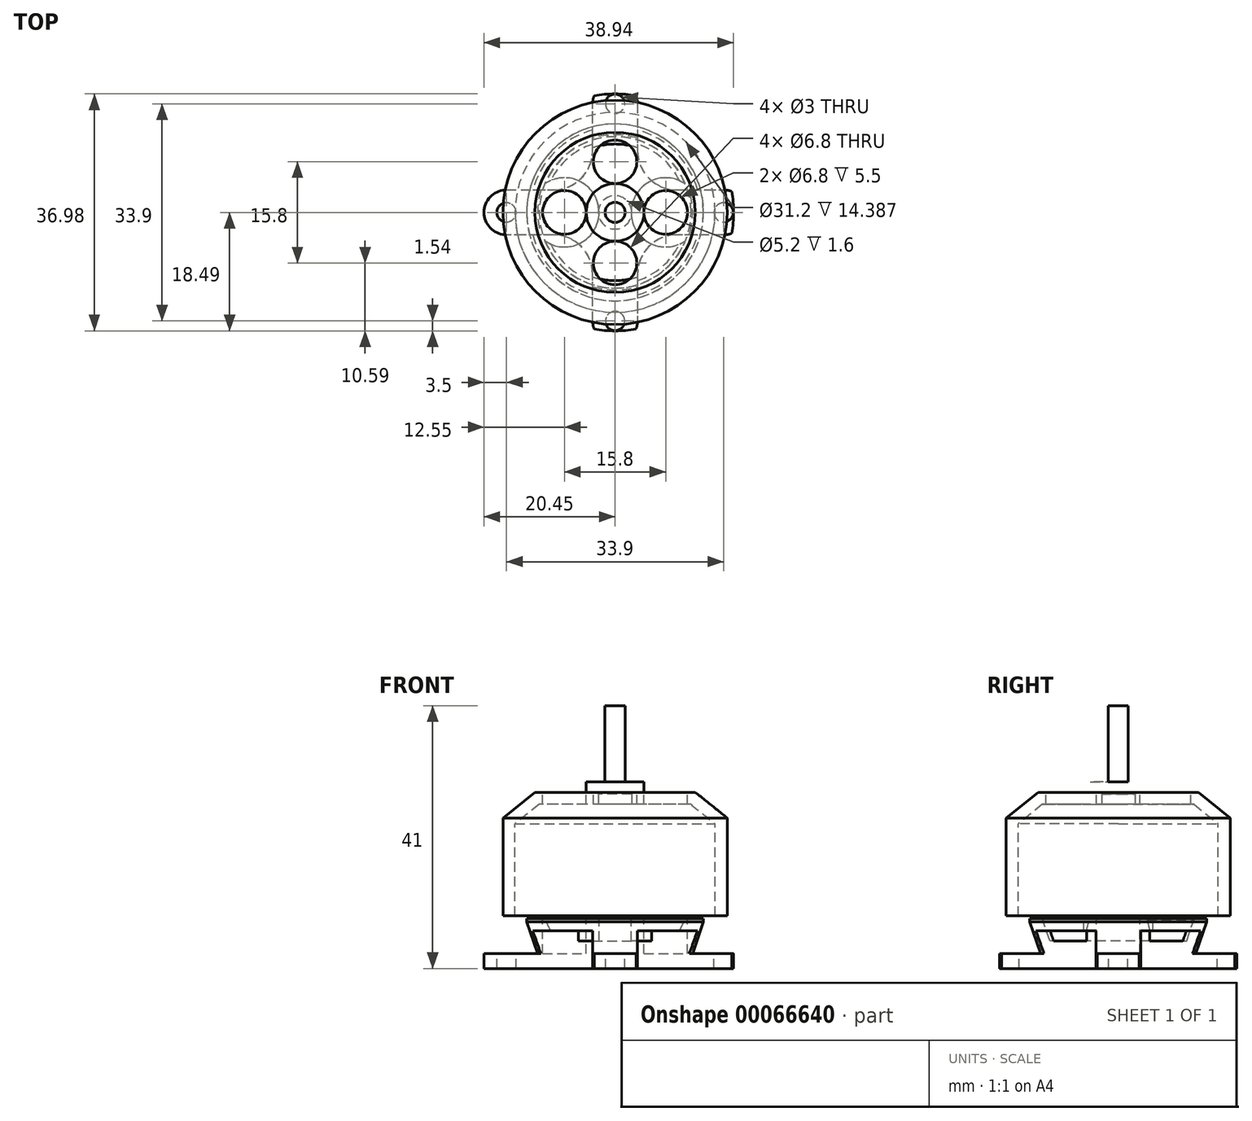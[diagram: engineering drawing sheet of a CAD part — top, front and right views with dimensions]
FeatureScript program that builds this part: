
annotation { "Feature Type Name" : "Feature", "Feature Type Description" : "" }
export const myFeature = defineFeature(function(context is Context, id is Id, definition is map)
    precondition{}
    {
        {
            var Q0;
            Q0=qCreatedBy(makeId("Top.planeOp"),FACE);
            var sketch = newSketch(context, id + "F0", { "sketchPlane" : qUnion([Q0])});
            skCircle(sketch, "E0", {"center": v(0, 0) * mm, "radius": 17.5 * mm});
            skCircle(sketch, "E1", {"center": v(0, 0) * mm, "radius": 1.57 * mm});
            skCircle(sketch, "E2", {"center": v(0, 0) * mm, "radius": 4.5 * mm});
            skCircle(sketch, "E3", {"center": v(0, 0) * mm, "radius": 8.78 * mm});
            skCircle(sketch, "E4", {"center": v(7.9, 0) * mm, "radius": 3.4 * mm});
            skCircle(sketch, "E5.1.0", {"center": v(0, 7.9) * mm, "radius": 3.4 * mm});
            skCircle(sketch, "E5.2.0", {"center": v(-7.9, 0) * mm, "radius": 3.4 * mm});
            skCircle(sketch, "E5.3.0", {"center": v(0, -7.9) * mm, "radius": 3.4 * mm});
            skSolve(sketch);
        }
        {
            var Q0;
            Q0=makeQuery(id+"F0.imprint","IMPRINT",FACE,{"disambiguationData":[TD([[makeQuery(id+"F0.imprint","IMPRINT",EDGE,{"derivedFrom":sQuery(id+"F0.wireOp",EDGE,"E0")}),1.0]])]});
            var Q1;
            {var subQ0=sQuery(id+"F0.wireOp",EDGE,"E5.1.0");var subQ1=sQuery(id+"F0.wireOp",EDGE,"E2");var subQ2=makeQuery(id+"F0.imprint","INTERSECT",VERTEX,{"derivedFrom":[subQ1,subQ0]});Q1=makeQuery(id+"F0.imprint","IMPRINT",FACE,{"disambiguationData":[TD([[makeQuery(id+"F0.imprint","IMPRINT",EDGE,{"disambiguationData":[TD([[subQ2,1.0]])],"derivedFrom":subQ1}),-1.0]])]});}
            var Q2;
            {var subQ0=sQuery(id+"F0.wireOp",EDGE,"E5.1.0");var subQ1=sQuery(id+"F0.wireOp",EDGE,"E2");var subQ2=makeQuery(id+"F0.imprint","INTERSECT",VERTEX,{"derivedFrom":[subQ1,subQ0]});Q2=makeQuery(id+"F0.imprint","IMPRINT",FACE,{"disambiguationData":[TD([[makeQuery(id+"F0.imprint","IMPRINT",EDGE,{"disambiguationData":[TD([[subQ2,-1.0]])],"derivedFrom":subQ1}),-1.0]])]});}
            var Q3;
            Q3=makeQuery(id+"F0.imprint","IMPRINT",FACE,{"disambiguationData":[TD([[makeQuery(id+"F0.imprint","IMPRINT",EDGE,{"derivedFrom":sQuery(id+"F0.wireOp",EDGE,"E1")}),-1.0]])]});
            var Q4;
            {var subQ0=sQuery(id+"F0.wireOp",EDGE,"E4");var subQ1=sQuery(id+"F0.wireOp",EDGE,"E2");var subQ2=makeQuery(id+"F0.imprint","INTERSECT",VERTEX,{"derivedFrom":[subQ1,subQ0]});Q4=makeQuery(id+"F0.imprint","IMPRINT",FACE,{"disambiguationData":[TD([[makeQuery(id+"F0.imprint","IMPRINT",EDGE,{"disambiguationData":[TD([[subQ2,1.0]])],"derivedFrom":subQ1}),-1.0]])]});}
            var Q5;
            {var subQ0=sQuery(id+"F0.wireOp",EDGE,"E5.2.0");var subQ1=sQuery(id+"F0.wireOp",EDGE,"E2");var subQ2=makeQuery(id+"F0.imprint","INTERSECT",VERTEX,{"derivedFrom":[subQ1,subQ0]});Q5=makeQuery(id+"F0.imprint","IMPRINT",FACE,{"disambiguationData":[TD([[makeQuery(id+"F0.imprint","IMPRINT",EDGE,{"disambiguationData":[TD([[subQ2,-1.0]])],"derivedFrom":subQ1}),-1.0]])]});}
            var Q6;
            Q6=makeQuery(id+"F0.imprint","IMPRINT",FACE,{"disambiguationData":[TD([[makeQuery(id+"F0.imprint","IMPRINT",EDGE,{"derivedFrom":sQuery(id+"F0.wireOp",EDGE,"E1")}),1.0]])]});
            var Q7;
            {var subQ0=sQuery(id+"F0.wireOp",EDGE,"E5.2.0");var subQ1=sQuery(id+"F0.wireOp",EDGE,"E3");var subQ2=makeQuery(id+"F0.imprint","INTERSECT",VERTEX,{"disambiguationData":[OD(0.0)],"derivedFrom":[subQ1,subQ0]});Q7=makeQuery(id+"F0.imprint","IMPRINT",FACE,{"disambiguationData":[TD([[makeQuery(id+"F0.imprint","IMPRINT",EDGE,{"disambiguationData":[TD([[subQ2,-1.0]])],"derivedFrom":subQ1}),-1.0]])]});}
            var Q8;
            {var subQ0=sQuery(id+"F0.wireOp",EDGE,"E5.2.0");var subQ1=sQuery(id+"F0.wireOp",EDGE,"E3");var subQ2=makeQuery(id+"F0.imprint","INTERSECT",VERTEX,{"disambiguationData":[OD(0.0)],"derivedFrom":[subQ1,subQ0]});Q8=makeQuery(id+"F0.imprint","IMPRINT",FACE,{"disambiguationData":[TD([[makeQuery(id+"F0.imprint","IMPRINT",EDGE,{"disambiguationData":[TD([[subQ2,-1.0]])],"derivedFrom":subQ1}),1.0]])]});}
            var Q9;
            {var subQ0=sQuery(id+"F0.wireOp",EDGE,"E5.1.0");var subQ1=sQuery(id+"F0.wireOp",EDGE,"E3");var subQ2=makeQuery(id+"F0.imprint","INTERSECT",VERTEX,{"disambiguationData":[OD(0.0)],"derivedFrom":[subQ1,subQ0]});Q9=makeQuery(id+"F0.imprint","IMPRINT",FACE,{"disambiguationData":[TD([[makeQuery(id+"F0.imprint","IMPRINT",EDGE,{"disambiguationData":[TD([[subQ2,-1.0]])],"derivedFrom":subQ1}),1.0]])]});}
            var Q10;
            {var subQ0=sQuery(id+"F0.wireOp",EDGE,"E4");var subQ1=sQuery(id+"F0.wireOp",EDGE,"E3");var subQ2=makeQuery(id+"F0.imprint","INTERSECT",VERTEX,{"disambiguationData":[OD(0.0)],"derivedFrom":[subQ1,subQ0]});Q10=makeQuery(id+"F0.imprint","IMPRINT",FACE,{"disambiguationData":[TD([[makeQuery(id+"F0.imprint","IMPRINT",EDGE,{"disambiguationData":[TD([[subQ2,1.0]])],"derivedFrom":subQ1}),1.0]])]});}
            var Q11;
            {var subQ0=sQuery(id+"F0.wireOp",EDGE,"E4");var subQ1=sQuery(id+"F0.wireOp",EDGE,"E3");var subQ2=makeQuery(id+"F0.imprint","INTERSECT",VERTEX,{"disambiguationData":[OD(0.0)],"derivedFrom":[subQ1,subQ0]});Q11=makeQuery(id+"F0.imprint","IMPRINT",FACE,{"disambiguationData":[TD([[makeQuery(id+"F0.imprint","IMPRINT",EDGE,{"disambiguationData":[TD([[subQ2,1.0]])],"derivedFrom":subQ1}),-1.0]])]});}
            var Q12;
            {var subQ0=sQuery(id+"F0.wireOp",EDGE,"E5.3.0");var subQ1=sQuery(id+"F0.wireOp",EDGE,"E3");var subQ2=makeQuery(id+"F0.imprint","INTERSECT",VERTEX,{"disambiguationData":[OD(0.0)],"derivedFrom":[subQ1,subQ0]});Q12=makeQuery(id+"F0.imprint","IMPRINT",FACE,{"disambiguationData":[TD([[makeQuery(id+"F0.imprint","IMPRINT",EDGE,{"disambiguationData":[TD([[subQ2,-1.0]])],"derivedFrom":subQ1}),1.0]])]});}
            var Q13;
            {var subQ0=sQuery(id+"F0.wireOp",EDGE,"E5.1.0");var subQ1=sQuery(id+"F0.wireOp",EDGE,"E3");var subQ2=makeQuery(id+"F0.imprint","INTERSECT",VERTEX,{"disambiguationData":[OD(0.0)],"derivedFrom":[subQ1,subQ0]});Q13=makeQuery(id+"F0.imprint","IMPRINT",FACE,{"disambiguationData":[TD([[makeQuery(id+"F0.imprint","IMPRINT",EDGE,{"disambiguationData":[TD([[subQ2,-1.0]])],"derivedFrom":subQ1}),-1.0]])]});}
            var Q14;
            {var subQ0=sQuery(id+"F0.wireOp",EDGE,"E5.3.0");var subQ1=sQuery(id+"F0.wireOp",EDGE,"E3");var subQ2=makeQuery(id+"F0.imprint","INTERSECT",VERTEX,{"disambiguationData":[OD(0.0)],"derivedFrom":[subQ1,subQ0]});Q14=makeQuery(id+"F0.imprint","IMPRINT",FACE,{"disambiguationData":[TD([[makeQuery(id+"F0.imprint","IMPRINT",EDGE,{"disambiguationData":[TD([[subQ2,-1.0]])],"derivedFrom":subQ1}),-1.0]])]});}
            extrude(context, id + "F1", {"entities" : qUnion([Q0, Q1, Q2, Q3, Q4, Q5, Q6, Q7, Q8, Q9, Q10, Q11, Q12, Q13, Q14]), "oppositeDirection" : true, "depth" : 19.3 * mm});
        }
        {
            var Q0;
            Q0=makeQuery(id+"F1.opExtrude","CAP_EDGE",EDGE,{"disambiguationData":[OSD([sQuery(id+"F0.wireOp",EDGE,"E0")])],"isStart":true});
            chamfer(context, id + "F2", {"entities" : qUnion([Q0]), "chamferType" : ChamferType.TWO_OFFSETS, "width1" : 5 * mm, "oppositeDirection" : false, "width2" : 4 * mm, "tangentPropagation" : true});
        }
        {
            var Q0;
            Q0=makeQuery(id+"F0.imprint","IMPRINT",FACE,{"disambiguationData":[TD([[makeQuery(id+"F0.imprint","IMPRINT",EDGE,{"derivedFrom":sQuery(id+"F0.wireOp",EDGE,"E1")}),-1.0]])]});
            extrude(context, id + "F3", {"entities" : qUnion([Q0]), "operationType" : NewBodyOperationType.ADD, "depth" : 1.6 * mm});
        }
        {
            var Q0;
            Q0=makeQuery(id+"F0.imprint","IMPRINT",FACE,{"disambiguationData":[TD([[makeQuery(id+"F0.imprint","IMPRINT",EDGE,{"derivedFrom":sQuery(id+"F0.wireOp",EDGE,"E1")}),1.0]])]});
            var Q1;
            Q1=sQuery(id+"F0.wireOp",EDGE,"E1");
            extrude(context, id + "F4", {"entities" : qUnion([Q0]), "operationType" : NewBodyOperationType.ADD, "surfaceEntities" : qUnion([Q1]), "depth" : 13.5 * mm});
        }
        {
            var Q0;
            Q0=makeQuery(id+"F1.opExtrude","CAP_FACE",FACE,{"disambiguationData":[OSD([sQuery(id+"F0.wireOp",EDGE,"E0")])],"isStart":false});
            shell(context, id + "F5", {"entities" : qUnion([Q0]), "thickness" : 1.9 * mm});
        }
        {
            var Q0;
            {var subQ0=sQuery(id+"F0.wireOp",EDGE,"E5.3.0");var subQ1=sQuery(id+"F0.wireOp",EDGE,"E3");var subQ2=makeQuery(id+"F0.imprint","INTERSECT",VERTEX,{"disambiguationData":[OD(0.0)],"derivedFrom":[subQ1,subQ0]});Q0=makeQuery(id+"F0.imprint","IMPRINT",FACE,{"disambiguationData":[TD([[makeQuery(id+"F0.imprint","IMPRINT",EDGE,{"disambiguationData":[TD([[subQ2,-1.0]])],"derivedFrom":subQ1}),-1.0]])]});}
            var Q1;
            {var subQ0=sQuery(id+"F0.wireOp",EDGE,"E5.3.0");var subQ1=sQuery(id+"F0.wireOp",EDGE,"E3");var subQ2=makeQuery(id+"F0.imprint","INTERSECT",VERTEX,{"disambiguationData":[OD(0.0)],"derivedFrom":[subQ1,subQ0]});Q1=makeQuery(id+"F0.imprint","IMPRINT",FACE,{"disambiguationData":[TD([[makeQuery(id+"F0.imprint","IMPRINT",EDGE,{"disambiguationData":[TD([[subQ2,-1.0]])],"derivedFrom":subQ1}),1.0]])]});}
            var Q2;
            {var subQ0=sQuery(id+"F0.wireOp",EDGE,"E4");var subQ1=sQuery(id+"F0.wireOp",EDGE,"E3");var subQ2=makeQuery(id+"F0.imprint","INTERSECT",VERTEX,{"disambiguationData":[OD(0.0)],"derivedFrom":[subQ1,subQ0]});Q2=makeQuery(id+"F0.imprint","IMPRINT",FACE,{"disambiguationData":[TD([[makeQuery(id+"F0.imprint","IMPRINT",EDGE,{"disambiguationData":[TD([[subQ2,1.0]])],"derivedFrom":subQ1}),-1.0]])]});}
            var Q3;
            {var subQ0=sQuery(id+"F0.wireOp",EDGE,"E4");var subQ1=sQuery(id+"F0.wireOp",EDGE,"E3");var subQ2=makeQuery(id+"F0.imprint","INTERSECT",VERTEX,{"disambiguationData":[OD(0.0)],"derivedFrom":[subQ1,subQ0]});Q3=makeQuery(id+"F0.imprint","IMPRINT",FACE,{"disambiguationData":[TD([[makeQuery(id+"F0.imprint","IMPRINT",EDGE,{"disambiguationData":[TD([[subQ2,1.0]])],"derivedFrom":subQ1}),1.0]])]});}
            var Q4;
            {var subQ0=sQuery(id+"F0.wireOp",EDGE,"E5.1.0");var subQ1=sQuery(id+"F0.wireOp",EDGE,"E3");var subQ2=makeQuery(id+"F0.imprint","INTERSECT",VERTEX,{"disambiguationData":[OD(0.0)],"derivedFrom":[subQ1,subQ0]});Q4=makeQuery(id+"F0.imprint","IMPRINT",FACE,{"disambiguationData":[TD([[makeQuery(id+"F0.imprint","IMPRINT",EDGE,{"disambiguationData":[TD([[subQ2,-1.0]])],"derivedFrom":subQ1}),1.0]])]});}
            var Q5;
            {var subQ0=sQuery(id+"F0.wireOp",EDGE,"E5.1.0");var subQ1=sQuery(id+"F0.wireOp",EDGE,"E3");var subQ2=makeQuery(id+"F0.imprint","INTERSECT",VERTEX,{"disambiguationData":[OD(0.0)],"derivedFrom":[subQ1,subQ0]});Q5=makeQuery(id+"F0.imprint","IMPRINT",FACE,{"disambiguationData":[TD([[makeQuery(id+"F0.imprint","IMPRINT",EDGE,{"disambiguationData":[TD([[subQ2,-1.0]])],"derivedFrom":subQ1}),-1.0]])]});}
            var Q6;
            {var subQ0=sQuery(id+"F0.wireOp",EDGE,"E5.2.0");var subQ1=sQuery(id+"F0.wireOp",EDGE,"E3");var subQ2=makeQuery(id+"F0.imprint","INTERSECT",VERTEX,{"disambiguationData":[OD(0.0)],"derivedFrom":[subQ1,subQ0]});Q6=makeQuery(id+"F0.imprint","IMPRINT",FACE,{"disambiguationData":[TD([[makeQuery(id+"F0.imprint","IMPRINT",EDGE,{"disambiguationData":[TD([[subQ2,-1.0]])],"derivedFrom":subQ1}),1.0]])]});}
            var Q7;
            {var subQ0=sQuery(id+"F0.wireOp",EDGE,"E5.2.0");var subQ1=sQuery(id+"F0.wireOp",EDGE,"E3");var subQ2=makeQuery(id+"F0.imprint","INTERSECT",VERTEX,{"disambiguationData":[OD(0.0)],"derivedFrom":[subQ1,subQ0]});Q7=makeQuery(id+"F0.imprint","IMPRINT",FACE,{"disambiguationData":[TD([[makeQuery(id+"F0.imprint","IMPRINT",EDGE,{"disambiguationData":[TD([[subQ2,-1.0]])],"derivedFrom":subQ1}),-1.0]])]});}
            var Q8;
            Q8=sQuery(id+"F0.wireOp",EDGE,"E5.3.0");
            extrude(context, id + "F6", {"entities" : qUnion([Q0, Q1, Q2, Q3, Q4, Q5, Q6, Q7]), "operationType" : NewBodyOperationType.REMOVE, "surfaceEntities" : qUnion([Q8]), "endBound" : BoundingType.THROUGH_ALL, "oppositeDirection" : true, "depth" : 25 * mm});
        }
        {
            var Q0;
            Q0=qCreatedBy(makeId("Top.planeOp"),FACE);
            var sketch = newSketch(context, id + "F7", { "sketchPlane" : qUnion([Q0])});
            skCircle(sketch, "E6", {"center": v(16.95, 0) * mm, "radius": 3.5 * mm});
            skCircle(sketch, "E7.1.0", {"center": v(0, 16.95) * mm, "radius": 3.5 * mm});
            skCircle(sketch, "E7.2.0", {"center": v(-16.95, 0) * mm, "radius": 3.5 * mm});
            skCircle(sketch, "E7.3.0", {"center": v(0, -16.95) * mm, "radius": 3.5 * mm});
            skPoint(sketch, "E7.center", {"position": v(0, 0) * mm});
            skLineSegment(sketch, "E8", {"start": v(16.95, 3.5) * mm, "end": v(9.66, 3.5) * mm});
            skLineSegment(sketch, "E9", {"start": v(3.5, 9.66) * mm, "end": v(3.5, 16.95) * mm});
            skPoint(sketch, "E10.visualSharp", {"position": v(3.5, 3.5) * mm});
            skArc(sketch, "E10.filletArc", {"start": v(3.5, 9.66) * mm, "mid": v(5.3, 5.3) * mm, "end": v(9.66, 3.5) * mm});
            skLineSegment(sketch, "E11.1.0", {"start": v(-3.5, 16.95) * mm, "end": v(-3.5, 9.66) * mm});
            skArc(sketch, "E11.1.1", {"start": v(-9.66, 3.5) * mm, "mid": v(-5.3, 5.3) * mm, "end": v(-3.5, 9.66) * mm});
            skLineSegment(sketch, "E11.1.2", {"start": v(-9.66, 3.5) * mm, "end": v(-16.95, 3.5) * mm});
            skLineSegment(sketch, "E11.2.0", {"start": v(-16.95, -3.5) * mm, "end": v(-9.66, -3.5) * mm});
            skArc(sketch, "E11.2.1", {"start": v(-3.5, -9.66) * mm, "mid": v(-5.3, -5.3) * mm, "end": v(-9.66, -3.5) * mm});
            skLineSegment(sketch, "E11.2.2", {"start": v(-3.5, -9.66) * mm, "end": v(-3.5, -16.95) * mm});
            skLineSegment(sketch, "E11.3.0", {"start": v(3.5, -16.95) * mm, "end": v(3.5, -9.66) * mm});
            skArc(sketch, "E11.3.1", {"start": v(9.66, -3.5) * mm, "mid": v(5.3, -5.3) * mm, "end": v(3.5, -9.66) * mm});
            skLineSegment(sketch, "E11.3.2", {"start": v(9.66, -3.5) * mm, "end": v(16.95, -3.5) * mm});
            skSolve(sketch);
        }
        {
            var Q0;
            Q0=makeQuery(id+"F1.opExtrude","CAP_FACE",FACE,{"disambiguationData":[OSD([sQuery(id+"F0.wireOp",EDGE,"E0")])],"isStart":false});
            cPlane(context, id + "F8", {"entities" : qUnion([Q0]), "cplaneType" : CPlaneType.OFFSET, "offset" : .4 * mm, "width" : 150 * mm, "height" : 150 * mm});
        }
        {
            var Q0;
            Q0=qCreatedBy(id+"F8.planeOp",FACE);
            var sketch = newSketch(context, id + "F9", { "sketchPlane" : qUnion([Q0])});
            skCircle(sketch, "E12", {"center": v(0, 0) * mm, "radius": 13.8 * mm});
            skCircle(sketch, "E13", {"center": v(0, 0) * mm, "radius": 1.57 * mm});
            skCircle(sketch, "E14", {"center": v(0, 0) * mm, "radius": 4.5 * mm});
            skCircle(sketch, "E15", {"center": v(0, 0) * mm, "radius": 8.78 * mm});
            skCircle(sketch, "E16", {"center": v(7.9, 0) * mm, "radius": 3.4 * mm});
            skCircle(sketch, "E17.1.0", {"center": v(0, 7.9) * mm, "radius": 3.4 * mm});
            skCircle(sketch, "E17.2.0", {"center": v(-7.9, 0) * mm, "radius": 3.4 * mm});
            skCircle(sketch, "E17.3.0", {"center": v(0, -7.9) * mm, "radius": 3.4 * mm});
            skSolve(sketch);
        }
        {
            var Q0;
            Q0=makeQuery(id+"F9.imprint","IMPRINT",FACE,{"disambiguationData":[TD([[makeQuery(id+"F9.imprint","IMPRINT",EDGE,{"derivedFrom":sQuery(id+"F9.wireOp",EDGE,"E12")}),1.0]])]});
            var Q1;
            {var subQ0=sQuery(id+"F9.wireOp",EDGE,"E17.3.0");var subQ1=sQuery(id+"F9.wireOp",EDGE,"E15");var subQ2=makeQuery(id+"F9.imprint","INTERSECT",VERTEX,{"disambiguationData":[OD(0.0)],"derivedFrom":[subQ1,subQ0]});Q1=makeQuery(id+"F9.imprint","IMPRINT",FACE,{"disambiguationData":[TD([[makeQuery(id+"F9.imprint","IMPRINT",EDGE,{"disambiguationData":[TD([[subQ2,-1.0]])],"derivedFrom":subQ1}),-1.0]])]});}
            var Q2;
            {var subQ0=sQuery(id+"F9.wireOp",EDGE,"E17.3.0");var subQ1=sQuery(id+"F9.wireOp",EDGE,"E15");var subQ2=makeQuery(id+"F9.imprint","INTERSECT",VERTEX,{"disambiguationData":[OD(0.0)],"derivedFrom":[subQ1,subQ0]});Q2=makeQuery(id+"F9.imprint","IMPRINT",FACE,{"disambiguationData":[TD([[makeQuery(id+"F9.imprint","IMPRINT",EDGE,{"disambiguationData":[TD([[subQ2,-1.0]])],"derivedFrom":subQ1}),1.0]])]});}
            var Q3;
            {var subQ0=sQuery(id+"F9.wireOp",EDGE,"E17.2.0");var subQ1=sQuery(id+"F9.wireOp",EDGE,"E15");var subQ2=makeQuery(id+"F9.imprint","INTERSECT",VERTEX,{"disambiguationData":[OD(0.0)],"derivedFrom":[subQ1,subQ0]});Q3=makeQuery(id+"F9.imprint","IMPRINT",FACE,{"disambiguationData":[TD([[makeQuery(id+"F9.imprint","IMPRINT",EDGE,{"disambiguationData":[TD([[subQ2,-1.0]])],"derivedFrom":subQ1}),-1.0]])]});}
            var Q4;
            {var subQ0=sQuery(id+"F9.wireOp",EDGE,"E17.2.0");var subQ1=sQuery(id+"F9.wireOp",EDGE,"E15");var subQ2=makeQuery(id+"F9.imprint","INTERSECT",VERTEX,{"disambiguationData":[OD(0.0)],"derivedFrom":[subQ1,subQ0]});Q4=makeQuery(id+"F9.imprint","IMPRINT",FACE,{"disambiguationData":[TD([[makeQuery(id+"F9.imprint","IMPRINT",EDGE,{"disambiguationData":[TD([[subQ2,-1.0]])],"derivedFrom":subQ1}),1.0]])]});}
            var Q5;
            {var subQ0=sQuery(id+"F9.wireOp",EDGE,"E17.1.0");var subQ1=sQuery(id+"F9.wireOp",EDGE,"E14");var subQ2=makeQuery(id+"F9.imprint","INTERSECT",VERTEX,{"derivedFrom":[subQ1,subQ0]});Q5=makeQuery(id+"F9.imprint","IMPRINT",FACE,{"disambiguationData":[TD([[makeQuery(id+"F9.imprint","IMPRINT",EDGE,{"disambiguationData":[TD([[subQ2,-1.0]])],"derivedFrom":subQ1}),-1.0]])]});}
            var Q6;
            {var subQ0=sQuery(id+"F9.wireOp",EDGE,"E17.2.0");var subQ1=sQuery(id+"F9.wireOp",EDGE,"E14");var subQ2=makeQuery(id+"F9.imprint","INTERSECT",VERTEX,{"derivedFrom":[subQ1,subQ0]});Q6=makeQuery(id+"F9.imprint","IMPRINT",FACE,{"disambiguationData":[TD([[makeQuery(id+"F9.imprint","IMPRINT",EDGE,{"disambiguationData":[TD([[subQ2,-1.0]])],"derivedFrom":subQ1}),-1.0]])]});}
            var Q7;
            Q7=makeQuery(id+"F9.imprint","IMPRINT",FACE,{"disambiguationData":[TD([[makeQuery(id+"F9.imprint","IMPRINT",EDGE,{"derivedFrom":sQuery(id+"F9.wireOp",EDGE,"E13")}),-1.0]])]});
            var Q8;
            Q8=makeQuery(id+"F9.imprint","IMPRINT",FACE,{"disambiguationData":[TD([[makeQuery(id+"F9.imprint","IMPRINT",EDGE,{"derivedFrom":sQuery(id+"F9.wireOp",EDGE,"E13")}),1.0]])]});
            var Q9;
            {var subQ0=sQuery(id+"F9.wireOp",EDGE,"E16");var subQ1=sQuery(id+"F9.wireOp",EDGE,"E14");var subQ2=makeQuery(id+"F9.imprint","INTERSECT",VERTEX,{"derivedFrom":[subQ1,subQ0]});Q9=makeQuery(id+"F9.imprint","IMPRINT",FACE,{"disambiguationData":[TD([[makeQuery(id+"F9.imprint","IMPRINT",EDGE,{"disambiguationData":[TD([[subQ2,1.0]])],"derivedFrom":subQ1}),-1.0]])]});}
            var Q10;
            {var subQ0=sQuery(id+"F9.wireOp",EDGE,"E16");var subQ1=sQuery(id+"F9.wireOp",EDGE,"E15");var subQ2=makeQuery(id+"F9.imprint","INTERSECT",VERTEX,{"disambiguationData":[OD(0.0)],"derivedFrom":[subQ1,subQ0]});Q10=makeQuery(id+"F9.imprint","IMPRINT",FACE,{"disambiguationData":[TD([[makeQuery(id+"F9.imprint","IMPRINT",EDGE,{"disambiguationData":[TD([[subQ2,1.0]])],"derivedFrom":subQ1}),1.0]])]});}
            var Q11;
            {var subQ0=sQuery(id+"F9.wireOp",EDGE,"E16");var subQ1=sQuery(id+"F9.wireOp",EDGE,"E15");var subQ2=makeQuery(id+"F9.imprint","INTERSECT",VERTEX,{"disambiguationData":[OD(0.0)],"derivedFrom":[subQ1,subQ0]});Q11=makeQuery(id+"F9.imprint","IMPRINT",FACE,{"disambiguationData":[TD([[makeQuery(id+"F9.imprint","IMPRINT",EDGE,{"disambiguationData":[TD([[subQ2,1.0]])],"derivedFrom":subQ1}),-1.0]])]});}
            var Q12;
            {var subQ0=sQuery(id+"F9.wireOp",EDGE,"E17.1.0");var subQ1=sQuery(id+"F9.wireOp",EDGE,"E14");var subQ2=makeQuery(id+"F9.imprint","INTERSECT",VERTEX,{"derivedFrom":[subQ1,subQ0]});Q12=makeQuery(id+"F9.imprint","IMPRINT",FACE,{"disambiguationData":[TD([[makeQuery(id+"F9.imprint","IMPRINT",EDGE,{"disambiguationData":[TD([[subQ2,1.0]])],"derivedFrom":subQ1}),-1.0]])]});}
            var Q13;
            {var subQ0=sQuery(id+"F9.wireOp",EDGE,"E17.1.0");var subQ1=sQuery(id+"F9.wireOp",EDGE,"E15");var subQ2=makeQuery(id+"F9.imprint","INTERSECT",VERTEX,{"disambiguationData":[OD(0.0)],"derivedFrom":[subQ1,subQ0]});Q13=makeQuery(id+"F9.imprint","IMPRINT",FACE,{"disambiguationData":[TD([[makeQuery(id+"F9.imprint","IMPRINT",EDGE,{"disambiguationData":[TD([[subQ2,-1.0]])],"derivedFrom":subQ1}),1.0]])]});}
            var Q14;
            {var subQ0=sQuery(id+"F9.wireOp",EDGE,"E17.1.0");var subQ1=sQuery(id+"F9.wireOp",EDGE,"E15");var subQ2=makeQuery(id+"F9.imprint","INTERSECT",VERTEX,{"disambiguationData":[OD(0.0)],"derivedFrom":[subQ1,subQ0]});Q14=makeQuery(id+"F9.imprint","IMPRINT",FACE,{"disambiguationData":[TD([[makeQuery(id+"F9.imprint","IMPRINT",EDGE,{"disambiguationData":[TD([[subQ2,-1.0]])],"derivedFrom":subQ1}),-1.0]])]});}
            extrude(context, id + "F10", {"entities" : qUnion([Q0, Q1, Q2, Q3, Q4, Q5, Q6, Q7, Q8, Q9, Q10, Q11, Q12, Q13, Q14]), "operationType" : NewBodyOperationType.ADD, "depth" : 5.5 * mm});
        }
        {
            var Q0;
            Q0=makeQuery(id+"F10.opExtrude","CAP_EDGE",EDGE,{"disambiguationData":[OSD([sQuery(id+"F9.wireOp",EDGE,"E12")])],"isStart":false});
            chamfer(context, id + "F11", {"entities" : qUnion([Q0]), "chamferType" : ChamferType.TWO_OFFSETS, "width1" : 5 * mm, "oppositeDirection" : true, "width2" : 1.7 * mm, "tangentPropagation" : true});
        }
        {
            var Q0;
            Q0=makeQuery(id+"F10.opExtrude","CAP_FACE",FACE,{"disambiguationData":[OSD([sQuery(id+"F9.wireOp",EDGE,"E12")])],"isStart":true});
            shell(context, id + "F12", {"entities" : qUnion([Q0]), "thickness" : 2 * mm});
        }
        {
            var Q0;
            Q0=makeQuery(id+"F10.opExtrude","CAP_FACE",FACE,{"disambiguationData":[OSD([sQuery(id+"F9.wireOp",EDGE,"E12")])],"isStart":false});
            cPlane(context, id + "F13", {"entities" : qUnion([Q0]), "cplaneType" : CPlaneType.OFFSET, "offset" : 0 * mm, "width" : 150 * mm, "height" : 150 * mm});
        }
        {
            var Q0;
            Q0=qCreatedBy(id+"F13.planeOp",FACE);
            var sketch = newSketch(context, id + "F14", { "sketchPlane" : qUnion([Q0])});
            skCircle(sketch, "E18", {"center": v(16.95, 0) * mm, "radius": 3.5 * mm});
            skCircle(sketch, "E19.1.0", {"center": v(0, 16.95) * mm, "radius": 3.5 * mm});
            skCircle(sketch, "E19.2.0", {"center": v(-16.95, 0) * mm, "radius": 3.5 * mm});
            skCircle(sketch, "E19.3.0", {"center": v(0, -16.95) * mm, "radius": 3.5 * mm});
            skPoint(sketch, "E19.center", {"position": v(0, 0) * mm});
            skLineSegment(sketch, "E20", {"start": v(16.95, 3.5) * mm, "end": v(9.66, 3.5) * mm});
            skLineSegment(sketch, "E21", {"start": v(3.5, 9.66) * mm, "end": v(3.5, 16.95) * mm});
            skPoint(sketch, "E22.visualSharp", {"position": v(3.5, 3.5) * mm});
            skArc(sketch, "E22.filletArc", {"start": v(3.5, 9.66) * mm, "mid": v(5.3, 5.3) * mm, "end": v(9.66, 3.5) * mm});
            skLineSegment(sketch, "E23.1.0", {"start": v(-3.5, 16.95) * mm, "end": v(-3.5, 9.66) * mm});
            skArc(sketch, "E23.1.1", {"start": v(-9.66, 3.5) * mm, "mid": v(-5.3, 5.3) * mm, "end": v(-3.5, 9.66) * mm});
            skLineSegment(sketch, "E23.1.2", {"start": v(-9.66, 3.5) * mm, "end": v(-16.95, 3.5) * mm});
            skLineSegment(sketch, "E23.2.0", {"start": v(-16.95, -3.5) * mm, "end": v(-9.66, -3.5) * mm});
            skArc(sketch, "E23.2.1", {"start": v(-3.5, -9.66) * mm, "mid": v(-5.3, -5.3) * mm, "end": v(-9.66, -3.5) * mm});
            skLineSegment(sketch, "E23.2.2", {"start": v(-3.5, -9.66) * mm, "end": v(-3.5, -16.95) * mm});
            skLineSegment(sketch, "E23.3.0", {"start": v(3.5, -16.95) * mm, "end": v(3.5, -9.66) * mm});
            skArc(sketch, "E23.3.1", {"start": v(9.66, -3.5) * mm, "mid": v(5.3, -5.3) * mm, "end": v(3.5, -9.66) * mm});
            skLineSegment(sketch, "E23.3.2", {"start": v(9.66, -3.5) * mm, "end": v(16.95, -3.5) * mm});
            skCircle(sketch, "E24", {"center": v(0, 0) * mm, "radius": 18.5 * mm});
            skCircle(sketch, "E25", {"center": v(16.95, 0) * mm, "radius": 1.5 * mm});
            skCircle(sketch, "E26.1.0", {"center": v(0, 16.95) * mm, "radius": 1.5 * mm});
            skCircle(sketch, "E26.2.0", {"center": v(-16.95, 0) * mm, "radius": 1.5 * mm});
            skCircle(sketch, "E26.3.0", {"center": v(0, -16.95) * mm, "radius": 1.5 * mm});
            skSolve(sketch);
        }
        {
            var Q0;
            {var subQ0=sQuery(id+"F14.wireOp",EDGE,"E23.1.1");Q0=makeQuery(id+"F14.imprint","IMPRINT",FACE,{"disambiguationData":[TD([[makeQuery(id+"F14.imprint","IMPRINT",EDGE,{"derivedFrom":subQ0}),1.0]])]});}
            var Q1;
            {var subQ0=sQuery(id+"F14.wireOp",EDGE,"E22.filletArc");Q1=makeQuery(id+"F14.imprint","IMPRINT",FACE,{"disambiguationData":[TD([[makeQuery(id+"F14.imprint","IMPRINT",EDGE,{"derivedFrom":subQ0}),1.0]])]});}
            var Q2;
            {var subQ0=sQuery(id+"F14.wireOp",EDGE,"E23.3.1");Q2=makeQuery(id+"F14.imprint","IMPRINT",FACE,{"disambiguationData":[TD([[makeQuery(id+"F14.imprint","IMPRINT",EDGE,{"derivedFrom":subQ0}),1.0]])]});}
            var Q3;
            {var subQ0=sQuery(id+"F14.wireOp",EDGE,"E23.2.1");Q3=makeQuery(id+"F14.imprint","IMPRINT",FACE,{"disambiguationData":[TD([[makeQuery(id+"F14.imprint","IMPRINT",EDGE,{"derivedFrom":subQ0}),1.0]])]});}
            extrude(context, id + "F15", {"entities" : qUnion([Q0, Q1, Q2, Q3]), "operationType" : NewBodyOperationType.REMOVE, "oppositeDirection" : true, "depth" : 3.6 * mm});
        }
        {
            var Q0;
            {var subQ1=sQuery(id+"F14.wireOp",EDGE,"E20");Q0=makeQuery(id+"F14.imprint","IMPRINT",FACE,{"disambiguationData":[TD([[makeQuery(id+"F14.imprint","IMPRINT",EDGE,{"derivedFrom":subQ1}),1.0]])]});}
            var Q1;
            Q1=makeQuery(id+"F14.imprint","IMPRINT",FACE,{"disambiguationData":[TD([[makeQuery(id+"F14.imprint","IMPRINT",EDGE,{"derivedFrom":sQuery(id+"F14.wireOp",EDGE,"E26.1.0")}),-1.0]])]});
            var Q2;
            {var subQ0=sQuery(id+"F14.wireOp",EDGE,"E24");var subQ1=sQuery(id+"F14.wireOp",EDGE,"E19.1.0");var subQ2=makeQuery(id+"F14.imprint","INTERSECT",VERTEX,{"disambiguationData":[OD(0.0)],"derivedFrom":[subQ1,subQ0]});Q2=makeQuery(id+"F14.imprint","IMPRINT",FACE,{"disambiguationData":[TD([[makeQuery(id+"F14.imprint","IMPRINT",EDGE,{"disambiguationData":[TD([[subQ2,1.0]])],"derivedFrom":subQ1}),1.0]])]});}
            var Q3;
            {var subQ0=sQuery(id+"F14.wireOp",EDGE,"E24");var subQ1=sQuery(id+"F14.wireOp",EDGE,"E19.2.0");var subQ2=makeQuery(id+"F14.imprint","INTERSECT",VERTEX,{"disambiguationData":[OD(0.0)],"derivedFrom":[subQ1,subQ0]});Q3=makeQuery(id+"F14.imprint","IMPRINT",FACE,{"disambiguationData":[TD([[makeQuery(id+"F14.imprint","IMPRINT",EDGE,{"disambiguationData":[TD([[subQ2,1.0]])],"derivedFrom":subQ1}),1.0]])]});}
            var Q4;
            Q4=makeQuery(id+"F14.imprint","IMPRINT",FACE,{"disambiguationData":[TD([[makeQuery(id+"F14.imprint","IMPRINT",EDGE,{"derivedFrom":sQuery(id+"F14.wireOp",EDGE,"E26.2.0")}),-1.0]])]});
            var Q5;
            Q5=makeQuery(id+"F14.imprint","IMPRINT",FACE,{"disambiguationData":[TD([[makeQuery(id+"F14.imprint","IMPRINT",EDGE,{"derivedFrom":sQuery(id+"F14.wireOp",EDGE,"E26.3.0")}),-1.0]])]});
            var Q6;
            {var subQ0=sQuery(id+"F14.wireOp",EDGE,"E24");var subQ1=sQuery(id+"F14.wireOp",EDGE,"E19.3.0");var subQ2=makeQuery(id+"F14.imprint","INTERSECT",VERTEX,{"disambiguationData":[OD(0.0)],"derivedFrom":[subQ1,subQ0]});Q6=makeQuery(id+"F14.imprint","IMPRINT",FACE,{"disambiguationData":[TD([[makeQuery(id+"F14.imprint","IMPRINT",EDGE,{"disambiguationData":[TD([[subQ2,1.0]])],"derivedFrom":subQ1}),1.0]])]});}
            var Q7;
            {var subQ0=sQuery(id+"F14.wireOp",EDGE,"E24");var subQ1=sQuery(id+"F14.wireOp",EDGE,"E18");var subQ2=makeQuery(id+"F14.imprint","INTERSECT",VERTEX,{"disambiguationData":[OD(0.0)],"derivedFrom":[subQ1,subQ0]});Q7=makeQuery(id+"F14.imprint","IMPRINT",FACE,{"disambiguationData":[TD([[makeQuery(id+"F14.imprint","IMPRINT",EDGE,{"disambiguationData":[TD([[subQ2,1.0]])],"derivedFrom":subQ1}),1.0]])]});}
            var Q8;
            Q8=makeQuery(id+"F14.imprint","IMPRINT",FACE,{"disambiguationData":[TD([[makeQuery(id+"F14.imprint","IMPRINT",EDGE,{"derivedFrom":sQuery(id+"F14.wireOp",EDGE,"E25")}),-1.0]])]});
            extrude(context, id + "F16", {"entities" : qUnion([Q0, Q1, Q2, Q3, Q4, Q5, Q6, Q7, Q8]), "operationType" : NewBodyOperationType.ADD, "depth" : 2.3 * mm});
        }
    });
